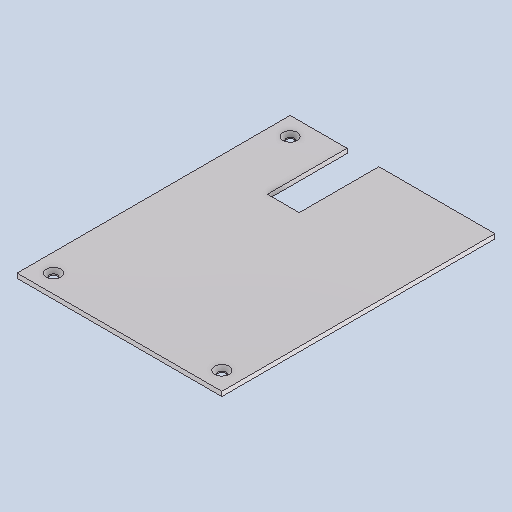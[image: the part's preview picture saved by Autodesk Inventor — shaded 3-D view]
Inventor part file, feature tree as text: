
AUTODESK INVENTOR PART (.ipt)
format: ipt  version: 2025 (Build 290162010, 162A)  size: 175,104 bytes
history: native  units: mm
features: sketch x2, extrude x1, hole x1, other x1
ambient origin geometry x8: Origin, YZ Plane, XZ Plane, XY Plane, X Axis, Y Axis, Z Axis, Center Point
bodies: Volumenkörper1 (feature_tree)
feature tree (5):
  extrude  "Extrusion1"  Depth=35.0mm
  hole  "Bohrung1"  [1 undecoded]
  sketch  "Skizze1"  dims[d0=14.0mm d1=35.0mm]
  sketch  "Skizze2"  dims[d2=25.0mm d3=0.0mm d4=0.0mm d5=8.0mm d6=8.0mm d7=8.0mm d8=8.0mm d9=3.4mm d10=8.0mm d11=6.3mm d12=2.0mm d13=90.0deg d14=8.0mm d15=20.594885mm]
  other  "item_47308_blech-al-2mm-naturfarben_120_90_high_1_1:1"
note: 1 required parameter value undecoded (feature->parameter linkage not recoverable at this tier; creation-order binding heuristic only, values carry confidence <= 0.55)
